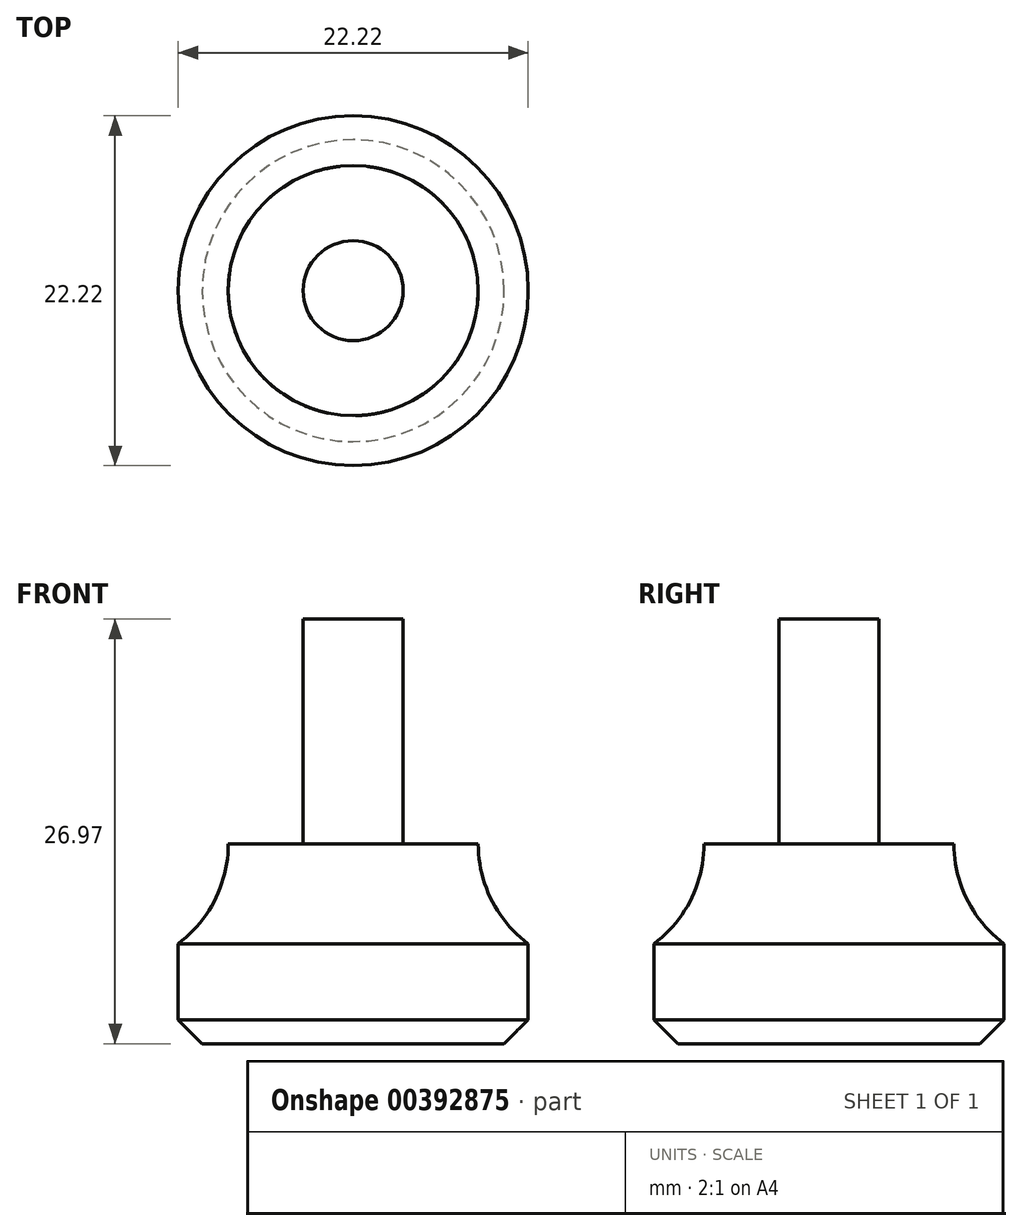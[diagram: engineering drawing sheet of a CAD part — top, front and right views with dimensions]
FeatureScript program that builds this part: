
annotation { "Feature Type Name" : "Feature", "Feature Type Description" : "" }
export const myFeature = defineFeature(function(context is Context, id is Id, definition is map)
    precondition{}
    {
        {
            var Q0;
            Q0=qCreatedBy(makeId("Right.planeOp"),FACE);
            var sketch = newSketch(context, id + "F0", { "sketchPlane" : qUnion([Q0])});
            skLineSegment(sketch, "E0.left", {"start": v(-11.11, 0) * mm, "end": v(-11.11, 6.35) * mm});
            skLineSegment(sketch, "E1", {"start": v(-3.18, 12.7) * mm, "end": v(-7.94, 12.7) * mm});
            skArc(sketch, "E2", {"start": v(-11.11, 6.35) * mm, "mid": v(-8.77, 9.15) * mm, "end": v(-7.94, 12.7) * mm});
            skLineSegment(sketch, "E3", {"start": v(-3.18, 12.7) * mm, "end": v(-3.18, 26.97) * mm});
            skLineSegment(sketch, "E4", {"start": v(-3.18, 26.97) * mm, "end": v(0, 26.97) * mm});
            skPoint(sketch, "E5.orphan", {"position": v(0, 12.7) * mm});
            skLineSegment(sketch, "E6", {"start": v(-11.11, 0) * mm, "end": v(0, 0) * mm});
            skLineSegment(sketch, "E7", {"start": v(0, 0) * mm, "end": v(0, 26.97) * mm});
            skSolve(sketch);
        }
        {
            var Q0;
            Q0=makeQuery(id+"F0.imprint","IMPRINT",FACE,{"disambiguationData":[TD([[makeQuery(id+"F0.imprint","IMPRINT",EDGE,{"derivedFrom":sQuery(id+"F0.wireOp",EDGE,"E0.left")}),-1.0]])]});
            var Q1;
            Q1=sQuery(id+"F0.wireOp",EDGE,"E7");
            revolve(context, id + "F1", {"entities" : qUnion([Q0]), "axis" : qUnion([Q1]), "revolveType" : RevolveType.FULL});
        }
        {
            var Q0;
            Q0=makeQuery(id+"F1.opRevolve","SWEPT_EDGE",EDGE,{"disambiguationData":[OSD([sQuery(id+"F0.wireOp",EDGE,"E0.left"),sQuery(id+"F0.wireOp",EDGE,"E6")])]});
            chamfer(context, id + "F2", {"entities" : qUnion([Q0]), "chamferType" : ChamferType.OFFSET_ANGLE, "width" : 1.52 * mm, "oppositeDirection" : false, "angle" : 45 * degree, "tangentPropagation" : true});
        }
    });
